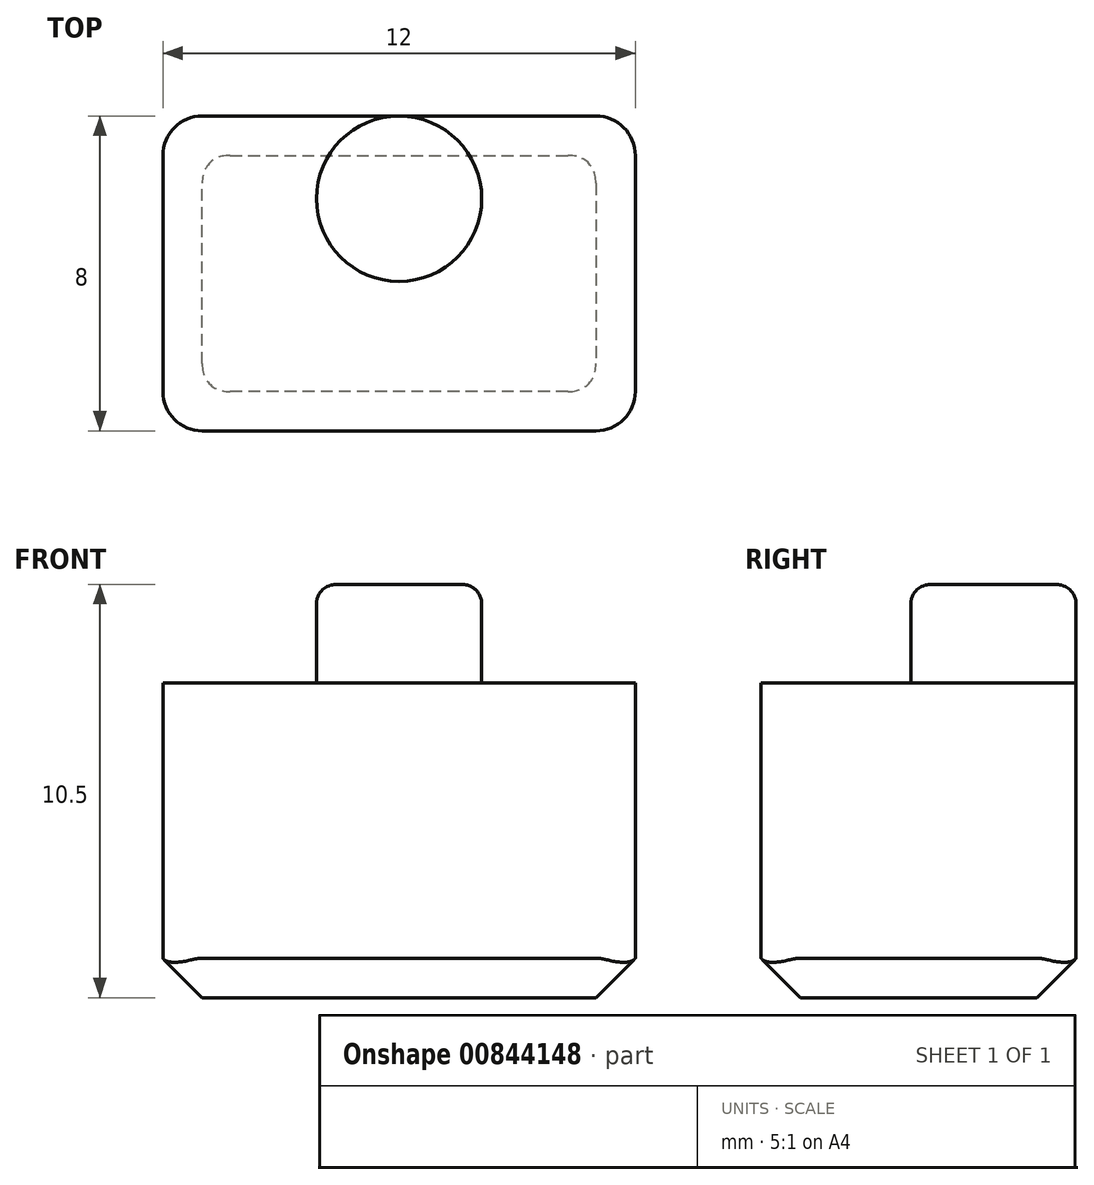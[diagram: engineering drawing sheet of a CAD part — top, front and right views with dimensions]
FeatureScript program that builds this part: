
annotation { "Feature Type Name" : "Feature", "Feature Type Description" : "" }
export const myFeature = defineFeature(function(context is Context, id is Id, definition is map)
    precondition{}
    {
        {
            var Q0;
            Q0=qCreatedBy(makeId("Top.planeOp"),FACE);
            var sketch = newSketch(context, id + "F0", { "sketchPlane" : qUnion([Q0])});
            skLineSegment(sketch, "E0.bottom", {"start": v(6, -4) * mm, "end": v(-6, -4) * mm});
            skLineSegment(sketch, "E0.top", {"start": v(6, 4) * mm, "end": v(-6, 4) * mm});
            skLineSegment(sketch, "E0.left", {"start": v(6, -4) * mm, "end": v(6, 4) * mm});
            skLineSegment(sketch, "E0.right", {"start": v(-6, -4) * mm, "end": v(-6, 4) * mm});
            skPoint(sketch, "E0.middle", {"position": v(0, 0) * mm});
            skCircle(sketch, "E1", {"center": v(0, 1.9) * mm, "radius": 2.1 * mm});
            skSolve(sketch);
        }
        {
            var Q0;
            Q0=qSketchRegion(id+"F0",true);
            extrude(context, id + "F1", {"entities" : qUnion([Q0]), "oppositeDirection" : true, "depth" : 8 * mm, "offsetDistance" : 25 * mm});
        }
        {
            var Q0;
            Q0=makeQuery(id+"F0.imprint","IMPRINT",FACE,{"disambiguationData":[TD([[makeQuery(id+"F0.imprint","IMPRINT",EDGE,{"derivedFrom":sQuery(id+"F0.wireOp",EDGE,"E1")}),1.0]])]});
            extrude(context, id + "F2", {"entities" : qUnion([Q0]), "operationType" : NewBodyOperationType.ADD, "depth" : 2.5 * mm, "offsetDistance" : 25 * mm});
        }
        {
            var Q0;
            Q0=makeQuery(id+"F2.opExtrude","CAP_EDGE",EDGE,{"disambiguationData":[OSD([sQuery(id+"F0.wireOp",EDGE,"E1")])],"isStart":false});
            fillet(context, id + "F3", {"entities" : qUnion([Q0]), "radius" : 0.5 * mm, "tangentPropagation" : true, "allowEdgeOverflow" : false});
        }
        {
            var Q0;
            Q0=makeQuery(id+"F1.opExtrude","CAP_EDGE",EDGE,{"disambiguationData":[OSD([sQuery(id+"F0.wireOp",EDGE,"E0.right")])],"isStart":false});
            var Q1;
            Q1=makeQuery(id+"F1.opExtrude","CAP_EDGE",EDGE,{"disambiguationData":[OSD([sQuery(id+"F0.wireOp",EDGE,"E0.bottom")])],"isStart":false});
            var Q2;
            Q2=makeQuery(id+"F1.opExtrude","CAP_EDGE",EDGE,{"disambiguationData":[OSD([sQuery(id+"F0.wireOp",EDGE,"E0.top")])],"isStart":false});
            var Q3;
            Q3=makeQuery(id+"F1.opExtrude","CAP_EDGE",EDGE,{"disambiguationData":[OSD([sQuery(id+"F0.wireOp",EDGE,"E0.left")])],"isStart":false});
            chamfer(context, id + "F4", {"entities" : qUnion([Q0, Q1, Q2, Q3]), "width" : 1 * mm, "tangentPropagation" : true});
        }
        {
            var Q0;
            Q0=makeQuery(id+"F1.opExtrude","SWEPT_EDGE",EDGE,{"disambiguationData":[OSD([sQuery(id+"F0.wireOp",EDGE,"E0.top"),sQuery(id+"F0.wireOp",EDGE,"E0.left")])]});
            var Q1;
            Q1=makeQuery(id+"F1.opExtrude","SWEPT_EDGE",EDGE,{"disambiguationData":[OSD([sQuery(id+"F0.wireOp",EDGE,"E0.top"),sQuery(id+"F0.wireOp",EDGE,"E0.right")])]});
            var Q2;
            Q2=makeQuery(id+"F4.opChamfer","BLEND_EDGE",EDGE,{"blendedFrom":[makeQuery(id+"F1.opExtrude","CAP_EDGE",EDGE,{"disambiguationData":[OSD([sQuery(id+"F0.wireOp",EDGE,"E0.top")])],"isStart":false}),makeQuery(id+"F1.opExtrude","CAP_EDGE",EDGE,{"disambiguationData":[OSD([sQuery(id+"F0.wireOp",EDGE,"E0.right")])],"isStart":false})],"blendedInto":[]});
            var Q3;
            Q3=makeQuery(id+"F4.opChamfer","BLEND_EDGE",EDGE,{"blendedFrom":[makeQuery(id+"F1.opExtrude","CAP_EDGE",EDGE,{"disambiguationData":[OSD([sQuery(id+"F0.wireOp",EDGE,"E0.top")])],"isStart":false}),makeQuery(id+"F1.opExtrude","CAP_EDGE",EDGE,{"disambiguationData":[OSD([sQuery(id+"F0.wireOp",EDGE,"E0.left")])],"isStart":false})],"blendedInto":[]});
            var Q4;
            Q4=makeQuery(id+"F4.opChamfer","BLEND_EDGE",EDGE,{"blendedFrom":[makeQuery(id+"F1.opExtrude","CAP_EDGE",EDGE,{"disambiguationData":[OSD([sQuery(id+"F0.wireOp",EDGE,"E0.bottom")])],"isStart":false}),makeQuery(id+"F1.opExtrude","CAP_EDGE",EDGE,{"disambiguationData":[OSD([sQuery(id+"F0.wireOp",EDGE,"E0.left")])],"isStart":false})],"blendedInto":[]});
            var Q5;
            Q5=makeQuery(id+"F4.opChamfer","BLEND_EDGE",EDGE,{"blendedFrom":[makeQuery(id+"F1.opExtrude","CAP_EDGE",EDGE,{"disambiguationData":[OSD([sQuery(id+"F0.wireOp",EDGE,"E0.bottom")])],"isStart":false}),makeQuery(id+"F1.opExtrude","CAP_EDGE",EDGE,{"disambiguationData":[OSD([sQuery(id+"F0.wireOp",EDGE,"E0.right")])],"isStart":false})],"blendedInto":[]});
            var Q6;
            Q6=makeQuery(id+"F1.opExtrude","SWEPT_EDGE",EDGE,{"disambiguationData":[OSD([sQuery(id+"F0.wireOp",EDGE,"E0.bottom"),sQuery(id+"F0.wireOp",EDGE,"E0.left")])]});
            var Q7;
            Q7=makeQuery(id+"F1.opExtrude","SWEPT_EDGE",EDGE,{"disambiguationData":[OSD([sQuery(id+"F0.wireOp",EDGE,"E0.bottom"),sQuery(id+"F0.wireOp",EDGE,"E0.right")])]});
            fillet(context, id + "F5", {"entities" : qUnion([Q0, Q1, Q2, Q3, Q4, Q5, Q6, Q7]), "radius" : 1 * mm, "tangentPropagation" : true, "allowEdgeOverflow" : false});
        }
    });
